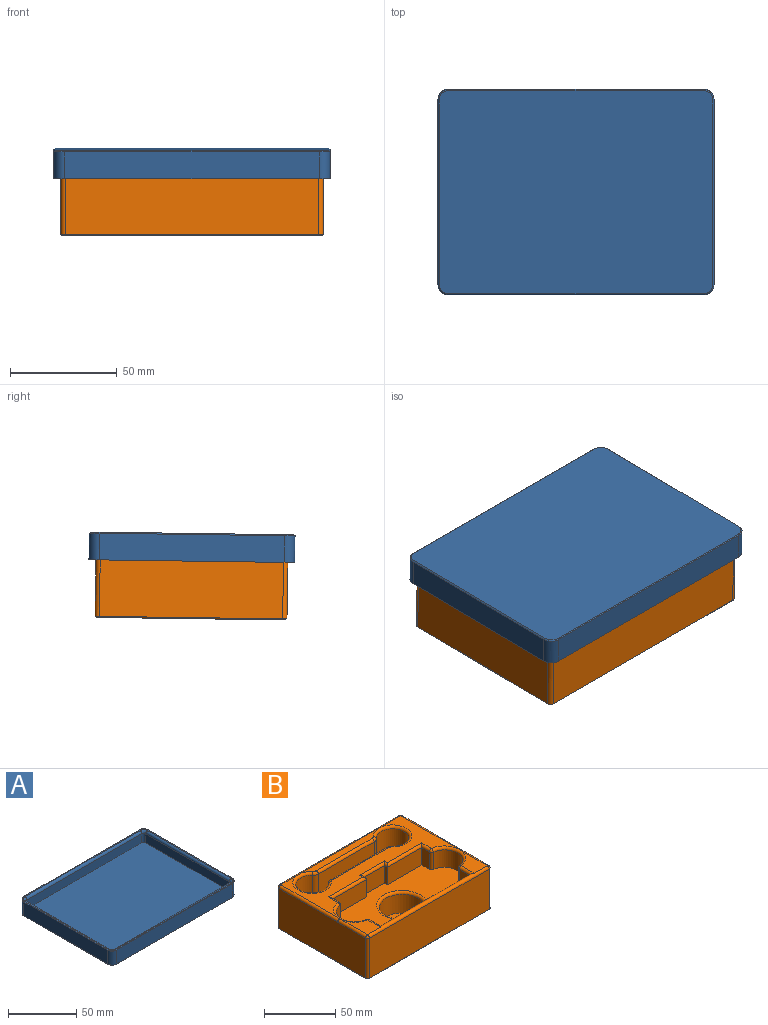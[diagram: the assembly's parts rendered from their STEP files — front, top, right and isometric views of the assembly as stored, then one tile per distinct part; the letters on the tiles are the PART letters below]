
ASSEMBLY  parts=2 mates=1
PART A: 35 faces, bbox 131.2x98.2x13 mm
  f0: plane 119.5x8mm, normal (0,-1,0), area 956mm2, adj f11,f17,f20,f21
  f1: plane 86.5x8mm, normal (-1,0,0), area 692mm2, adj f14,f18,f20,f21
  f2: plane 119.5x8mm, normal (0,1,0), area 956mm2, adj f9,f13,f14,f21
  f3: plane 119.5x12.5mm, normal (0,1,0), area 1493.8mm2, adj f8,f23,f26,f32
  f4: plane 86.5x12.5mm, normal (-1,0,0), area 1081.2mm2, adj f8,f23,f24,f28
  f5: plane 119.5x12.5mm, normal (0,-1,0), area 1493.8mm2, adj f8,f24,f25,f29
  f6: plane 86.5x12.5mm, normal (1,0,0), area 1081.2mm2, adj f8,f25,f26,f33
  f7: plane 86.5x8mm, normal (1,0,0), area 692mm2, adj f9,f11,f12,f21
  f8: plane 129.5x96.5mm, normal (0,0,1), area 440.3mm2, adj f3,f4,f5,f6,f10,f12,f13,f15
  f9: cylinder r=2mm len=8mm, axis (0,0,-1), area 25.1mm2, adj f2,f7,f10,f21
  f10: torus R=4mm, axis (0,0,1), area 13.5mm2, adj f8,f9,f12,f13
  f11: cylinder r=2mm len=8mm, axis (0,0,1), area 25.1mm2, adj f0,f7,f15,f21
  f12: cylinder r=2mm len=86.5mm, axis (0,-1,0), area 271.7mm2, adj f7,f8,f10,f15
  f13: cylinder r=2mm len=119.5mm, axis (1,0,0), area 375.4mm2, adj f2,f8,f10,f16
  f14: cylinder r=2mm len=8mm, axis (0,0,1), area 25.1mm2, adj f1,f2,f16,f21
  f15: torus R=4mm, axis (0,0,1), area 13.5mm2, adj f8,f11,f12,f17
  f16: torus R=4mm, axis (0,0,1), area 13.5mm2, adj f8,f13,f14,f18
  f17: cylinder r=2mm len=119.5mm, axis (-1,0,0), area 375.4mm2, adj f0,f8,f15,f19
  f18: cylinder r=2mm len=86.5mm, axis (0,1,0), area 271.7mm2, adj f1,f8,f16,f19
  f19: torus R=4mm, axis (0,0,1), area 13.5mm2, adj f8,f17,f18,f20
  f20: cylinder r=2mm len=8mm, axis (0,0,-1), area 25.1mm2, adj f0,f1,f19,f21
  f21: plane 123.5x90.5mm, normal (0,0,1), area 11173.3mm2, adj f0,f1,f2,f7,f9,f11,f14,f20
  f22: plane 128.5x95.5mm, normal (0,0,-1), area 12254.4mm2, adj f27,f28,f29,f30,f31,f32,f33,f34
  f23: cylinder r=5mm len=12.5mm, axis (0,0,1), area 98.2mm2, adj f3,f4,f8,f30
  f24: cylinder r=5mm len=12.5mm, axis (0,0,-1), area 98.2mm2, adj f4,f5,f8,f27
  f25: cylinder r=5mm len=12.5mm, axis (0,0,1), area 98.2mm2, adj f5,f6,f8,f31
  f26: cylinder r=5mm len=12.5mm, axis (0,0,-1), area 98.2mm2, adj f3,f6,f8,f34
  f27: cone r=4.5mm half-angle=45deg, axis (0,0,1), area 5.3mm2, adj f22,f24,f28,f29
  f28: plane 86.5x0.5mm, normal (-0.71,0,-0.71), area 61.2mm2, adj f4,f22,f27,f30
  f29: plane 119.5x0.5mm, normal (0,-0.71,-0.71), area 84.5mm2, adj f5,f22,f27,f31
  f30: cone r=4.5mm half-angle=45deg, axis (0,0,1), area 5.3mm2, adj f22,f23,f28,f32
  f31: cone r=4.5mm half-angle=45deg, axis (0,0,1), area 5.3mm2, adj f22,f25,f29,f33
  f32: plane 119.5x0.5mm, normal (0,0.71,-0.71), area 84.5mm2, adj f3,f22,f30,f34
  f33: plane 86.5x0.5mm, normal (0.71,0,-0.71), area 61.2mm2, adj f6,f22,f31,f34
  f34: cone r=4.5mm half-angle=45deg, axis (0,0,1), area 5.3mm2, adj f22,f26,f32,f33
PART B: 85 faces, bbox 124.5x90.6x37 mm
  f0: plane 119x58.29mm, normal (0,0,1), area 1944.8mm2, adj f29,f30,f32,f34,f36,f38,f40,f41
  f1: plane 80x5.46mm, normal (0,0,1), area 353.5mm2, adj f29,f31,f32,f57,f62,f64
  f2: plane 27.36x13mm, normal (0,0,1), area 211.2mm2, adj f37,f39,f41,f54
  f3: plane 27.36x13mm, normal (0,0,1), area 211.2mm2, adj f34,f35,f37,f48
  f4: plane 119x34.5mm, normal (0,1,0), area 4105.5mm2, adj f52,f57,f60,f79
  f5: plane 86x34.5mm, normal (-1,0,0), area 2967mm2, adj f49,f54,f56,f58,f60,f83
  f6: plane 119x34.5mm, normal (0,-1,0), area 4105.5mm2, adj f37,f46,f49,f82
  f7: plane 86x34.5mm, normal (1,0,0), area 2967mm2, adj f46,f48,f50,f52,f53,f78
  f8: plane 122x89mm, normal (0,0,-1), area 10856.1mm2, adj f77,f78,f79,f80,f81,f82,f83,f84
  f9: plane 15x10.67mm, normal (1,0,0), area 160.1mm2, adj f10,f21,f39,f75
  f10: plane 89x15mm, normal (0,1,0), area 1335mm2, adj f9,f11,f21,f37
  f11: plane 15x10.67mm, normal (-1,0,0), area 160.1mm2, adj f10,f21,f35,f69
  f12: cylinder r=13mm len=25.77mm, axis (0,0,1), area 560.5mm2, adj f21,f34,f69,f71
  f13: plane 15x7.59mm, normal (-1,0,0), area 113.9mm2, adj f14,f21,f36,f71
  f14: plane 34.05x15mm, normal (0,-1,0), area 510.8mm2, adj f13,f15,f21,f38
  f15: plane 15x3mm, normal (-1,0,0), area 45mm2, adj f14,f16,f21,f40
  f16: plane 20.9x15mm, normal (0,-1,0), area 313.5mm2, adj f15,f17,f21,f42
  f17: plane 15x3mm, normal (1,0,0), area 45mm2, adj f16,f18,f21,f44
  f18: plane 34.05x15mm, normal (0,-1,0), area 510.8mm2, adj f17,f19,f21,f45
  f19: plane 15x7.59mm, normal (1,0,0), area 113.9mm2, adj f18,f21,f43,f73
  f20: cylinder r=13mm len=25.77mm, axis (0,0,1), area 560.5mm2, adj f21,f41,f73,f75
  f21: plane 115x51mm, normal (0,0,1), area 3850.6mm2, adj f9,f10,f11,f12,f13,f14,f15,f16
  f22: cylinder r=16mm len=32mm, axis (0,0,1), area 1608.5mm2, adj f23,f33
  f23: plane 32x32mm, normal (0,0,1), area 804.2mm2, adj f22
  f24: cylinder r=11.46mm len=26mm, axis (0,0,1), area 1435.7mm2, adj f28,f29,f61,f67
  f25: plane 55.52x26mm, normal (0,1,0), area 1443.4mm2, adj f28,f30,f65,f67
  f26: cylinder r=11.46mm len=26mm, axis (0,0,1), area 1435.7mm2, adj f28,f32,f63,f65
  f27: plane 55.52x26mm, normal (0,-1,0), area 1443.4mm2, adj f28,f31,f61,f63
  f28: plane 102.92x22.92mm, normal (0,0,1), area 1526.3mm2, adj f24,f25,f26,f27,f61,f63,f65,f67
  f29: torus R=13.46mm, axis (0,0,1), area 184.5mm2, adj f0,f1,f24,f62,f68
  f30: cylinder r=2mm len=55.52mm, axis (-1,0,0), area 174.4mm2, adj f0,f25,f66,f68
  f31: cylinder r=2mm len=55.52mm, axis (1,0,0), area 174.4mm2, adj f1,f27,f62,f64
  f32: torus R=13.46mm, axis (0,0,1), area 184.5mm2, adj f0,f1,f26,f64,f66
  f33: torus R=18mm, axis (0,0,1), area 330.2mm2, adj f21,f22
  f34: torus R=15mm, axis (0,0,1), area 124mm2, adj f0,f3,f12,f50,f70,f72
  f35: cylinder r=2mm len=12.67mm, axis (0,-1,0), area 35.8mm2, adj f3,f11,f37,f70
  f36: cylinder r=2mm len=9.59mm, axis (0,-1,0), area 26.1mm2, adj f0,f13,f38,f72
  f37: cylinder r=2mm len=119mm, axis (-1,0,0), area 658mm2, adj f2,f3,f6,f10,f35,f39,f47,f51
  f38: cylinder r=2mm len=36.05mm, axis (1,0,0), area 107mm2, adj f0,f14,f36,f40
  f39: cylinder r=2mm len=12.67mm, axis (0,1,0), area 35.8mm2, adj f2,f9,f37,f76
  f40: cylinder r=2mm len=5mm, axis (0,-1,0), area 9.4mm2, adj f0,f15,f38,f42
  f41: torus R=15mm, axis (0,0,1), area 124mm2, adj f0,f2,f20,f56,f74,f76
  f42: cylinder r=2mm len=24.9mm, axis (1,0,0), area 70.2mm2, adj f0,f16,f40,f44
  f43: cylinder r=2mm len=9.59mm, axis (0,1,0), area 26.1mm2, adj f0,f19,f45,f74
  f44: cylinder r=2mm len=5mm, axis (0,1,0), area 9.4mm2, adj f0,f17,f42,f45
  f45: cylinder r=2mm len=36.05mm, axis (1,0,0), area 107mm2, adj f0,f18,f43,f44
  f46: cylinder r=2mm len=34.5mm, axis (0,0,1), area 108.4mm2, adj f6,f7,f47,f80
  f47: sphere r=2mm, area 6.3mm2, adj f37,f46,f48
  f48: cylinder r=2mm len=27.36mm, axis (0,-1,0), area 86mm2, adj f3,f7,f47,f50
  f49: cylinder r=2mm len=34.5mm, axis (0,0,-1), area 108.4mm2, adj f5,f6,f51,f84
  f50: bspline ~2.03x2.03mm, area 1.1mm2, adj f7,f34,f48,f53
  f51: sphere r=2mm, area 6.3mm2, adj f37,f49,f54
  f52: cylinder r=2mm len=34.5mm, axis (0,0,-1), area 108.4mm2, adj f4,f7,f55,f77
  f53: cylinder r=2mm len=58.29mm, axis (0,-1,0), area 183.1mm2, adj f0,f7,f50,f55
  f54: cylinder r=2mm len=27.36mm, axis (0,1,0), area 86mm2, adj f2,f5,f51,f56
  f55: sphere r=2mm, area 6.3mm2, adj f52,f53,f57
  f56: bspline ~2.03x2.03mm, area 1.1mm2, adj f5,f41,f54,f58
  f57: cylinder r=2mm len=119mm, axis (1,0,0), area 373.8mm2, adj f0,f1,f4,f55,f59
  f58: cylinder r=2mm len=58.29mm, axis (0,1,0), area 183.1mm2, adj f0,f5,f56,f59
  f59: sphere r=2mm, area 6.3mm2, adj f57,f58,f60
  f60: cylinder r=2mm len=34.5mm, axis (0,0,1), area 108.4mm2, adj f4,f5,f59,f81
  f61: cylinder r=5mm len=26mm, axis (0,0,1), area 109mm2, adj f24,f27,f28,f62
  f62: torus R=3mm, axis (0,0,1), area 11.3mm2, adj f1,f29,f31,f61
  f63: cylinder r=5mm len=26mm, axis (0,0,1), area 109mm2, adj f26,f27,f28,f64
  f64: torus R=3mm, axis (0,0,1), area 11.3mm2, adj f1,f31,f32,f63
  f65: cylinder r=5mm len=26mm, axis (0,0,1), area 109mm2, adj f25,f26,f28,f66
  f66: torus R=3mm, axis (0,0,1), area 11.3mm2, adj f0,f30,f32,f65
  f67: cylinder r=5mm len=26mm, axis (0,0,1), area 109mm2, adj f24,f25,f28,f68
  f68: torus R=3mm, axis (0,0,1), area 11.3mm2, adj f0,f29,f30,f67
  f69: cylinder r=2mm len=15mm, axis (0,0,1), area 43.1mm2, adj f11,f12,f21,f70
  f70: sphere r=2mm, area 5.7mm2, adj f34,f35,f69
  f71: cylinder r=2mm len=15mm, axis (0,0,1), area 43.1mm2, adj f12,f13,f21,f72
  f72: sphere r=2mm, area 5.7mm2, adj f34,f36,f71
  f73: cylinder r=2mm len=15mm, axis (0,0,1), area 43.1mm2, adj f19,f20,f21,f74
  f74: sphere r=2mm, area 5.7mm2, adj f41,f43,f73
  f75: cylinder r=2mm len=15mm, axis (0,0,1), area 43.1mm2, adj f9,f20,f21,f76
  f76: sphere r=2mm, area 5.7mm2, adj f39,f41,f75
  f77: cone r=1.5mm half-angle=45deg, axis (0,0,1), area 1.9mm2, adj f8,f52,f78,f79
  f78: plane 86x0.5mm, normal (0.71,0,-0.71), area 60.8mm2, adj f7,f8,f77,f80
  f79: plane 119x0.5mm, normal (0,0.71,-0.71), area 84.1mm2, adj f4,f8,f77,f81
  f80: cone r=1.5mm half-angle=45deg, axis (0,0,1), area 1.9mm2, adj f8,f46,f78,f82
  f81: cone r=1.5mm half-angle=45deg, axis (0,0,1), area 1.9mm2, adj f8,f60,f79,f83
  f82: plane 119x0.5mm, normal (0,-0.71,-0.71), area 84.1mm2, adj f6,f8,f80,f84
  f83: plane 86x0.5mm, normal (-0.71,0,-0.71), area 60.8mm2, adj f5,f8,f81,f84
  f84: cone r=1.5mm half-angle=45deg, axis (0,0,1), area 1.9mm2, adj f8,f49,f82,f83
PLACE A rot(axis=(-1,0,0),179.2deg) t=(73.4,11.95,-20.02)mm
PLACE B rot(axis=(1,0,0),0.8deg) t=(11.74,56.67,-56.41)mm
MATE slider A.f22 <-> B.f8  axis (0,-0.01,1) through (11.65,72.46,-16.19)mm
